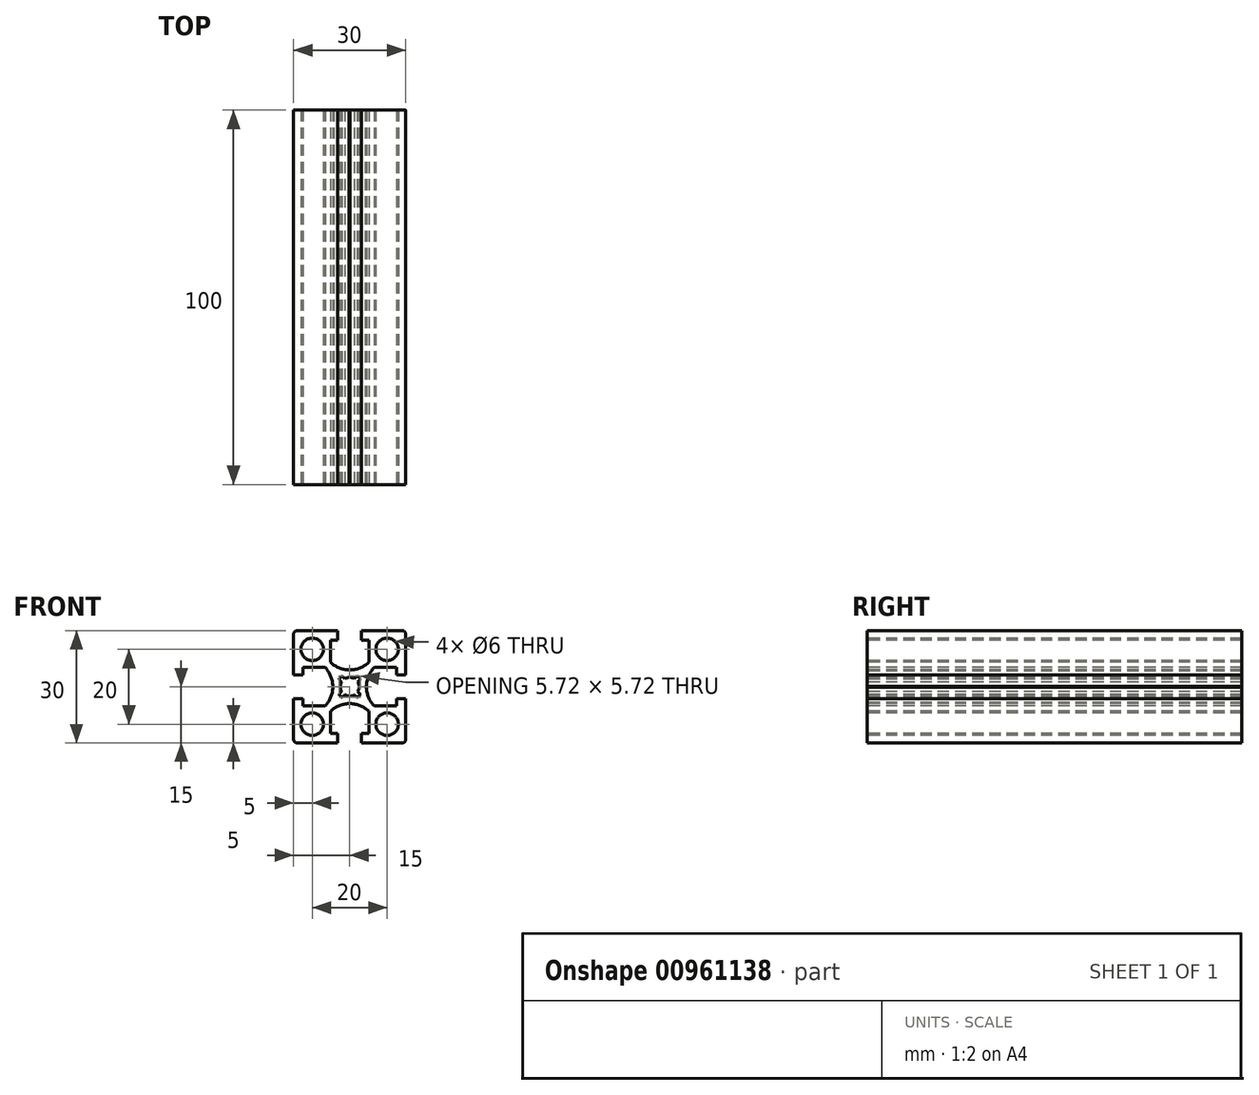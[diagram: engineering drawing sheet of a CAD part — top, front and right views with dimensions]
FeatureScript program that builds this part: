
annotation { "Feature Type Name" : "Feature", "Feature Type Description" : "" }
export const myFeature = defineFeature(function(context is Context, id is Id, definition is map)
    precondition{}
    {
        {
            var Q0;
            Q0=qCreatedBy(makeId("Front.planeOp"),FACE);
            var sketch = newSketch(context, id + "F0", { "sketchPlane" : qUnion([Q0])});
            skLineSegment(sketch, "E0", {"start": v(-15, 0) * mm, "end": v(15, 0) * mm, "construction": true});
            skLineSegment(sketch, "E1", {"start": v(0, 15) * mm, "end": v(0, -15) * mm, "construction": true});
            skLineSegment(sketch, "E2.bottom", {"start": v(-15, 15) * mm, "end": v(15, 15) * mm});
            skLineSegment(sketch, "E2.top", {"start": v(-15, -15) * mm, "end": v(15, -15) * mm});
            skLineSegment(sketch, "E2.left", {"start": v(-15, 15) * mm, "end": v(-15, -15) * mm});
            skLineSegment(sketch, "E2.right", {"start": v(15, 15) * mm, "end": v(15, -15) * mm});
            skPoint(sketch, "E3", {"position": v(0, 15) * mm});
            skCircle(sketch, "E4", {"center": v(-10, 10) * mm, "radius": 3 * mm});
            skCircle(sketch, "E5.1.0.0", {"center": v(10, 10) * mm, "radius": 3 * mm});
            skLineSegment(sketch, "E5.direction1", {"start": v(-10, 10) * mm, "end": v(10, 10) * mm, "construction": true});
            skLineSegment(sketch, "E6", {"start": v(-10, 10) * mm, "end": v(-10, -10) * mm, "construction": true});
            skLineSegment(sketch, "E7", {"start": v(-10, -10) * mm, "end": v(10, -10) * mm, "construction": true});
            skLineSegment(sketch, "E8", {"start": v(10, -10) * mm, "end": v(10, 10) * mm, "construction": true});
            skCircle(sketch, "E9", {"center": v(-10, -10) * mm, "radius": 3 * mm});
            skCircle(sketch, "E10", {"center": v(10, -10) * mm, "radius": 3 * mm});
            skLineSegment(sketch, "E11", {"start": v(-3.15, 15) * mm, "end": v(-3.15, 12.5) * mm});
            skLineSegment(sketch, "E12", {"start": v(-3.15, 12.5) * mm, "end": v(-5.15, 12.5) * mm});
            skLineSegment(sketch, "E13", {"start": v(-5.15, 12.5) * mm, "end": v(-5.15, 6.55) * mm});
            skLineSegment(sketch, "E14", {"start": v(-5.15, 6.55) * mm, "end": v(5.15, 6.55) * mm, "construction": true});
            skLineSegment(sketch, "E15", {"start": v(5.15, 6.55) * mm, "end": v(5.15, 12.5) * mm});
            skLineSegment(sketch, "E16", {"start": v(5.15, 12.5) * mm, "end": v(3.15, 12.5) * mm});
            skLineSegment(sketch, "E17", {"start": v(3.15, 12.5) * mm, "end": v(3.15, 15) * mm});
            skArc(sketch, "E18", {"start": v(-5.15, 6.55) * mm, "mid": v(0, 4.5) * mm, "end": v(5.15, 6.55) * mm});
            skPoint(sketch, "E19", {"position": v(0, 4.5) * mm});
            skArc(sketch, "E20.MirrorCS", {"start": v(-5.15, -6.55) * mm, "mid": v(0, -4.5) * mm, "end": v(5.15, -6.55) * mm});
            skLineSegment(sketch, "E21.MirrorCS", {"start": v(-5.15, -12.5) * mm, "end": v(-5.15, -6.55) * mm});
            skLineSegment(sketch, "E22.MirrorCS", {"start": v(-3.15, -12.5) * mm, "end": v(-5.15, -12.5) * mm});
            skLineSegment(sketch, "E23.MirrorCS", {"start": v(-3.15, -15) * mm, "end": v(-3.15, -12.5) * mm});
            skLineSegment(sketch, "E24.MirrorCS", {"start": v(3.15, -12.5) * mm, "end": v(3.15, -15) * mm});
            skLineSegment(sketch, "E25.MirrorCS", {"start": v(5.15, -12.5) * mm, "end": v(3.15, -12.5) * mm});
            skLineSegment(sketch, "E26.MirrorCS", {"start": v(5.15, -6.55) * mm, "end": v(5.15, -12.5) * mm});
            skLineSegment(sketch, "E27", {"start": v(-15, 3.15) * mm, "end": v(-12.5, 3.15) * mm});
            skLineSegment(sketch, "E28", {"start": v(-12.5, 3.15) * mm, "end": v(-12.5, 5.15) * mm});
            skLineSegment(sketch, "E29", {"start": v(-12.5, 5.15) * mm, "end": v(-6.55, 5.15) * mm});
            skLineSegment(sketch, "E30", {"start": v(-6.55, 5.15) * mm, "end": v(-6.55, -5.15) * mm, "construction": true});
            skLineSegment(sketch, "E31", {"start": v(-6.55, -5.15) * mm, "end": v(-12.5, -5.15) * mm});
            skLineSegment(sketch, "E32", {"start": v(-12.5, -5.15) * mm, "end": v(-12.5, -3.15) * mm});
            skLineSegment(sketch, "E33", {"start": v(-12.5, -3.15) * mm, "end": v(-15, -3.15) * mm});
            skArc(sketch, "E34", {"start": v(-6.55, -5.15) * mm, "mid": v(-4.5, 0) * mm, "end": v(-6.55, 5.15) * mm});
            skArc(sketch, "E35.MirrorCS", {"start": v(6.55, -5.15) * mm, "mid": v(4.5, 0) * mm, "end": v(6.55, 5.15) * mm});
            skLineSegment(sketch, "E36.MirrorCS", {"start": v(12.5, 5.15) * mm, "end": v(6.55, 5.15) * mm});
            skLineSegment(sketch, "E37.MirrorCS", {"start": v(6.55, -5.15) * mm, "end": v(12.5, -5.15) * mm});
            skLineSegment(sketch, "E38.MirrorCS", {"start": v(12.5, -5.15) * mm, "end": v(12.5, -3.15) * mm});
            skLineSegment(sketch, "E39.MirrorCS", {"start": v(12.5, -3.15) * mm, "end": v(15, -3.15) * mm});
            skLineSegment(sketch, "E40.MirrorCS", {"start": v(15, 3.15) * mm, "end": v(12.5, 3.15) * mm});
            skLineSegment(sketch, "E41.MirrorCS", {"start": v(12.5, 3.15) * mm, "end": v(12.5, 5.15) * mm});
            skArc(sketch, "E42", {"start": v(-2.14, 1.3) * mm, "mid": v(-2.5, 0) * mm, "end": v(-2.14, -1.3) * mm});
            skLineSegment(sketch, "E43", {"start": v(-10, 10) * mm, "end": v(10, -10) * mm, "construction": true});
            skLineSegment(sketch, "E44", {"start": v(-10, -10) * mm, "end": v(10, 10) * mm, "construction": true});
            skLineSegment(sketch, "E45", {"start": v(-2.86, -2.01) * mm, "end": v(-2.14, -1.3) * mm});
            skLineSegment(sketch, "E46", {"start": v(2.01, 2.86) * mm, "end": v(2.86, 2.01) * mm, "construction": true});
            skLineSegment(sketch, "E47", {"start": v(2.86, 2.01) * mm, "end": v(2.14, 1.3) * mm});
            skLineSegment(sketch, "E48", {"start": v(-2.01, -2.86) * mm, "end": v(-2.86, -2.01) * mm, "construction": true});
            skLineSegment(sketch, "E49", {"start": v(-2.01, 2.86) * mm, "end": v(-1.3, 2.14) * mm});
            skLineSegment(sketch, "E50", {"start": v(2.86, -2.01) * mm, "end": v(2.01, -2.86) * mm, "construction": true});
            skLineSegment(sketch, "E51", {"start": v(2.01, -2.86) * mm, "end": v(1.3, -2.14) * mm});
            skLineSegment(sketch, "E52", {"start": v(-2.86, 2.01) * mm, "end": v(-2.01, 2.86) * mm, "construction": true});
            skArc(sketch, "E53", {"start": v(-2.01, 2.86) * mm, "mid": v(-2.47, 2.47) * mm, "end": v(-2.86, 2.01) * mm});
            skArc(sketch, "E54.trimOffspring", {"start": v(2.86, 2.01) * mm, "mid": v(2.47, 2.47) * mm, "end": v(2.01, 2.86) * mm});
            skArc(sketch, "E55.trimOffspring", {"start": v(2.01, -2.86) * mm, "mid": v(2.47, -2.47) * mm, "end": v(2.86, -2.01) * mm});
            skArc(sketch, "E56.trimOffspring", {"start": v(-2.86, -2.01) * mm, "mid": v(-2.47, -2.47) * mm, "end": v(-2.01, -2.86) * mm});
            skArc(sketch, "E57.trimOffspring", {"start": v(1.3, 2.14) * mm, "mid": v(0, 2.5) * mm, "end": v(-1.3, 2.14) * mm});
            skLineSegment(sketch, "E58.trimOffspring", {"start": v(1.3, 2.14) * mm, "end": v(2.01, 2.86) * mm});
            skLineSegment(sketch, "E59.trimOffspring", {"start": v(2.14, -1.3) * mm, "end": v(2.86, -2.01) * mm});
            skLineSegment(sketch, "E60.trimOffspring", {"start": v(-2.14, 1.3) * mm, "end": v(-2.86, 2.01) * mm});
            skLineSegment(sketch, "E61.trimOffspring", {"start": v(-1.3, -2.14) * mm, "end": v(-2.01, -2.86) * mm});
            skArc(sketch, "E62.trimOffspring", {"start": v(2.14, -1.3) * mm, "mid": v(2.5, 0) * mm, "end": v(2.14, 1.3) * mm});
            skArc(sketch, "E63.trimOffspring", {"start": v(-1.3, -2.14) * mm, "mid": v(0, -2.5) * mm, "end": v(1.3, -2.14) * mm});
            skLineSegment(sketch, "E64", {"start": v(-0.15, 4.5) * mm, "end": v(0, 4.2) * mm});
            skLineSegment(sketch, "E65", {"start": v(0, 4.2) * mm, "end": v(0.15, 4.5) * mm});
            skLineSegment(sketch, "E66.MirrorCS", {"start": v(0, -4.2) * mm, "end": v(0.15, -4.5) * mm});
            skLineSegment(sketch, "E67.MirrorCS", {"start": v(-0.15, -4.5) * mm, "end": v(0, -4.2) * mm});
            skLineSegment(sketch, "E68", {"start": v(-4.5, 0.15) * mm, "end": v(-4.2, 0) * mm});
            skLineSegment(sketch, "E69", {"start": v(-4.2, 0) * mm, "end": v(-4.5, -0.15) * mm});
            skLineSegment(sketch, "E70.MirrorCS", {"start": v(4.2, 0) * mm, "end": v(4.5, -0.15) * mm});
            skLineSegment(sketch, "E71.MirrorCS", {"start": v(4.5, 0.15) * mm, "end": v(4.2, 0) * mm});
            skSolve(sketch);
        }
        {
            var Q0;
            Q0=makeQuery(id+"F0.imprint","IMPRINT",FACE,{"disambiguationData":[TD([[makeQuery(id+"F0.imprint","IMPRINT",EDGE,{"derivedFrom":sQuery(id+"F0.wireOp",EDGE,"E4")}),-1.0]])]});
            extrude(context, id + "F1", {"entities" : qUnion([Q0]), "oppositeDirection" : true, "depth" : 100 * mm, "offsetDistance" : 25 * mm});
        }
        {
            var Q0;
            Q0=makeQuery(id+"F1.opExtrude","SWEPT_EDGE",EDGE,{"disambiguationData":[OSD([sQuery(id+"F0.wireOp",EDGE,"E2.bottom"),sQuery(id+"F0.wireOp",EDGE,"E2.right")])]});
            var Q1;
            Q1=makeQuery(id+"F1.opExtrude","SWEPT_EDGE",EDGE,{"disambiguationData":[OSD([sQuery(id+"F0.wireOp",EDGE,"E2.bottom"),sQuery(id+"F0.wireOp",EDGE,"E2.left")])]});
            var Q2;
            Q2=makeQuery(id+"F1.opExtrude","SWEPT_EDGE",EDGE,{"disambiguationData":[OSD([sQuery(id+"F0.wireOp",EDGE,"E2.top"),sQuery(id+"F0.wireOp",EDGE,"E2.left")])]});
            var Q3;
            Q3=makeQuery(id+"F1.opExtrude","SWEPT_EDGE",EDGE,{"disambiguationData":[OSD([sQuery(id+"F0.wireOp",EDGE,"E2.top"),sQuery(id+"F0.wireOp",EDGE,"E2.right")])]});
            fillet(context, id + "F2", {"entities" : qUnion([Q0, Q1, Q2, Q3]), "radius" : 1 * mm, "tangentPropagation" : true, "allowEdgeOverflow" : false});
        }
    });
